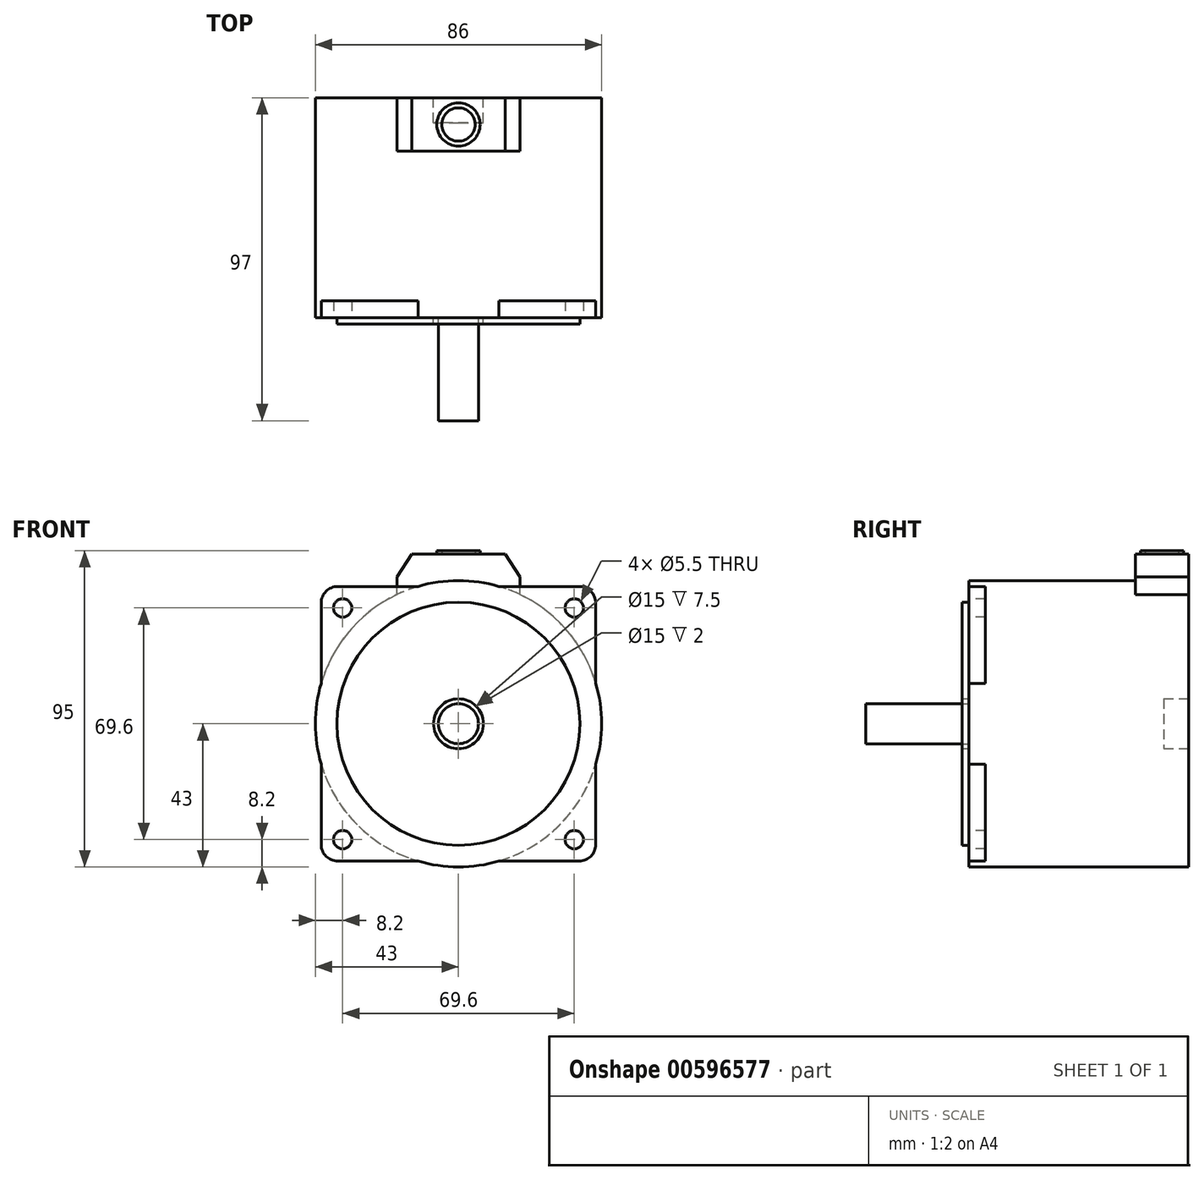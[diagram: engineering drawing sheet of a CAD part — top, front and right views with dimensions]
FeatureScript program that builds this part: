
annotation { "Feature Type Name" : "Feature", "Feature Type Description" : "" }
export const myFeature = defineFeature(function(context is Context, id is Id, definition is map)
    precondition{}
    {
        {
            var Q0;
            Q0=qCreatedBy(makeId("Front.planeOp"),FACE);
            var sketch = newSketch(context, id + "F0", { "sketchPlane" : qUnion([Q0])});
            skCircle(sketch, "E0", {"center": v(0, 0) * mm, "radius": 43 * mm});
            skSolve(sketch);
        }
        {
            var Q0;
            Q0 = qSketchRegion(id + "F0", true);
            extrude(context, id + "F1", {"entities" : qUnion([Q0]), "depth" : 61 * mm, "offsetDistance" : 25 * mm});
        }
        {
            var Q0;
            Q0=makeQuery(id+"F1.opExtrude","CAP_FACE",FACE,{"disambiguationData":[OSD([sQuery(id+"F0.wireOp",EDGE,"E0")])],"isStart":true});
            var sketch = newSketch(context, id + "F2", { "sketchPlane" : qUnion([Q0])});
            skCircle(sketch, "E1", {"center": v(0, 0) * mm, "radius": 7.5 * mm});
            skSolve(sketch);
        }
        {
            var Q0;
            Q0=makeQuery(id+"F2.imprint","IMPRINT",FACE,{"disambiguationData":[TD([[makeQuery(id+"F2.imprint","IMPRINT",EDGE,{"derivedFrom":sQuery(id+"F2.wireOp",EDGE,"E1")}),1.0]])]});
            extrude(context, id + "F3", {"entities" : qUnion([Q0]), "operationType" : NewBodyOperationType.REMOVE, "oppositeDirection" : true, "depth" : 7.5 * mm, "offsetDistance" : 25 * mm});
        }
        {
            var Q0;
            Q0=makeQuery(id+"F1.opExtrude","CAP_FACE",FACE,{"disambiguationData":[OSD([sQuery(id+"F0.wireOp",EDGE,"E0")])],"isStart":false});
            var sketch = newSketch(context, id + "F4", { "sketchPlane" : qUnion([Q0])});
            skLineSegment(sketch, "E2.bottom", {"start": v(-41.25, -41.25) * mm, "end": v(-12.14, -41.25) * mm});
            skLineSegment(sketch, "E2.top", {"start": v(-41.25, 41.25) * mm, "end": v(-12.14, 41.25) * mm});
            skLineSegment(sketch, "E2.left", {"start": v(-41.25, -41.25) * mm, "end": v(-41.25, -12.14) * mm});
            skLineSegment(sketch, "E2.right", {"start": v(41.25, -41.25) * mm, "end": v(41.25, -12.14) * mm});
            skCircle(sketch, "E3", {"center": v(0, 0) * mm, "radius": 43 * mm});
            skLineSegment(sketch, "E4.trimOffspring", {"start": v(12.14, 41.25) * mm, "end": v(41.25, 41.25) * mm});
            skLineSegment(sketch, "E5.trimOffspring", {"start": v(-41.25, 12.14) * mm, "end": v(-41.25, 41.25) * mm});
            skLineSegment(sketch, "E6.trimOffspring", {"start": v(41.25, 12.14) * mm, "end": v(41.25, 41.25) * mm});
            skLineSegment(sketch, "E7.trimOffspring", {"start": v(12.14, -41.25) * mm, "end": v(41.25, -41.25) * mm});
            skSolve(sketch);
        }
        {
            var Q0;
            Q0 = qSketchRegion(id + "F4", true);
            extrude(context, id + "F5", {"entities" : qUnion([Q0]), "operationType" : NewBodyOperationType.ADD, "depth" : 5 * mm, "offsetDistance" : 25 * mm});
        }
        {
            var Q0;
            Q0=makeQuery(id+"F5.opExtrude","SWEPT_EDGE",EDGE,{"disambiguationData":[OSD([sQuery(id+"F4.wireOp",EDGE,"E2.right"),sQuery(id+"F4.wireOp",EDGE,"E7.trimOffspring")])]});
            var Q1;
            Q1=makeQuery(id+"F5.opExtrude","SWEPT_EDGE",EDGE,{"disambiguationData":[OSD([sQuery(id+"F4.wireOp",EDGE,"E2.bottom"),sQuery(id+"F4.wireOp",EDGE,"E2.left")])]});
            var Q2;
            Q2=makeQuery(id+"F5.opExtrude","SWEPT_EDGE",EDGE,{"disambiguationData":[OSD([sQuery(id+"F4.wireOp",EDGE,"E2.top"),sQuery(id+"F4.wireOp",EDGE,"E5.trimOffspring")])]});
            var Q3;
            Q3=makeQuery(id+"F5.opExtrude","SWEPT_EDGE",EDGE,{"disambiguationData":[OSD([sQuery(id+"F4.wireOp",EDGE,"E4.trimOffspring"),sQuery(id+"F4.wireOp",EDGE,"E6.trimOffspring")])]});
            fillet(context, id + "F6", {"entities" : qUnion([Q0, Q1, Q2, Q3]), "radius" : 5 * mm, "tangentPropagation" : true, "allowEdgeOverflow" : false});
        }
        {
            var Q0;
            Q0=makeQuery(id+"F5.opExtrude","CAP_FACE",FACE,{"disambiguationData":[OSD([sQuery(id+"F4.wireOp",EDGE,"E2.bottom"),sQuery(id+"F4.wireOp",EDGE,"E2.top"),sQuery(id+"F4.wireOp",EDGE,"E2.left"),sQuery(id+"F4.wireOp",EDGE,"E2.right"),sQuery(id+"F4.wireOp",EDGE,"E3"),sQuery(id+"F4.wireOp",EDGE,"E4.trimOffspring"),sQuery(id+"F4.wireOp",EDGE,"E5.trimOffspring"),sQuery(id+"F4.wireOp",EDGE,"E6.trimOffspring"),sQuery(id+"F4.wireOp",EDGE,"E7.trimOffspring")])],"isStart":false});
            var sketch = newSketch(context, id + "F7", { "sketchPlane" : qUnion([Q0])});
            skCircle(sketch, "E8", {"center": v(-34.8, 34.8) * mm, "radius": 2.75 * mm});
            skCircle(sketch, "E9.1.0.0", {"center": v(34.8, 34.8) * mm, "radius": 2.75 * mm});
            skLineSegment(sketch, "E9.direction1", {"start": v(-34.8, 34.8) * mm, "end": v(34.8, 34.8) * mm, "construction": true});
            skCircle(sketch, "E10.MirrorC", {"center": v(34.8, -34.8) * mm, "radius": 2.75 * mm});
            skCircle(sketch, "E11.MirrorC", {"center": v(-34.8, -34.8) * mm, "radius": 2.75 * mm});
            skSolve(sketch);
        }
        {
            var Q0;
            Q0 = qSketchRegion(id + "F7", true);
            extrude(context, id + "F8", {"entities" : qUnion([Q0]), "operationType" : NewBodyOperationType.REMOVE, "endBound" : BoundingType.THROUGH_ALL, "oppositeDirection" : true, "depth" : 25 * mm, "offsetDistance" : 25 * mm});
        }
        {
            var Q0;
            Q0=makeQuery(id+"F5.opExtrude","CAP_FACE",FACE,{"disambiguationData":[OSD([sQuery(id+"F4.wireOp",EDGE,"E2.bottom"),sQuery(id+"F4.wireOp",EDGE,"E2.top"),sQuery(id+"F4.wireOp",EDGE,"E2.left"),sQuery(id+"F4.wireOp",EDGE,"E2.right"),sQuery(id+"F4.wireOp",EDGE,"E3"),sQuery(id+"F4.wireOp",EDGE,"E4.trimOffspring"),sQuery(id+"F4.wireOp",EDGE,"E5.trimOffspring"),sQuery(id+"F4.wireOp",EDGE,"E6.trimOffspring"),sQuery(id+"F4.wireOp",EDGE,"E7.trimOffspring")])],"isStart":false});
            var sketch = newSketch(context, id + "F9", { "sketchPlane" : qUnion([Q0])});
            skCircle(sketch, "E12", {"center": v(0, 0) * mm, "radius": 36.5 * mm});
            skCircle(sketch, "E13", {"center": v(0, 0) * mm, "radius": 7.5 * mm});
            skSolve(sketch);
        }
        {
            var Q0;
            Q0=makeQuery(id+"F9.imprint","IMPRINT",FACE,{"disambiguationData":[TD([[makeQuery(id+"F9.imprint","IMPRINT",EDGE,{"derivedFrom":sQuery(id+"F9.wireOp",EDGE,"E12")}),1.0]])]});
            extrude(context, id + "F10", {"entities" : qUnion([Q0]), "operationType" : NewBodyOperationType.ADD, "depth" : 2 * mm, "offsetDistance" : 25 * mm});
        }
        {
            var Q0;
            Q0=makeQuery(id+"F10.boolean.opBoolean","SPLIT",FACE,{"disambiguationData":[TD([makeQuery(id+"F10.opExtrude","SWEPT_FACE",FACE,{"disambiguationData":[OSD([sQuery(id+"F9.wireOp",EDGE,"E13")])]})])],"derivedFrom":makeQuery(id+"F5.opExtrude","CAP_FACE",FACE,{"disambiguationData":[OSD([sQuery(id+"F4.wireOp",EDGE,"E2.bottom"),sQuery(id+"F4.wireOp",EDGE,"E2.top"),sQuery(id+"F4.wireOp",EDGE,"E2.left"),sQuery(id+"F4.wireOp",EDGE,"E2.right"),sQuery(id+"F4.wireOp",EDGE,"E3"),sQuery(id+"F4.wireOp",EDGE,"E4.trimOffspring"),sQuery(id+"F4.wireOp",EDGE,"E5.trimOffspring"),sQuery(id+"F4.wireOp",EDGE,"E6.trimOffspring"),sQuery(id+"F4.wireOp",EDGE,"E7.trimOffspring")])],"isStart":false})});
            var sketch = newSketch(context, id + "F11", { "sketchPlane" : qUnion([Q0])});
            skCircle(sketch, "E14", {"center": v(0, 0) * mm, "radius": 6 * mm});
            skSolve(sketch);
        }
        {
            var Q0;
            Q0 = qSketchRegion(id + "F11", true);
            extrude(context, id + "F12", {"entities" : qUnion([Q0]), "operationType" : NewBodyOperationType.ADD, "depth" : 31 * mm, "offsetDistance" : 25 * mm});
        }
        {
            var Q0;
            Q0=makeQuery(id+"F1.opExtrude","CAP_FACE",FACE,{"disambiguationData":[OSD([sQuery(id+"F0.wireOp",EDGE,"E0")])],"isStart":true});
            var sketch = newSketch(context, id + "F13", { "sketchPlane" : qUnion([Q0])});
            skLineSegment(sketch, "E15", {"start": v(0, 0) * mm, "end": v(0, 51) * mm, "construction": true});
            skLineSegment(sketch, "E16.0", {"start": v(-18.5, 38.82) * mm, "end": v(-18.5, 44.1) * mm});
            skLineSegment(sketch, "E17.MirrorCS", {"start": v(18.5, 38.82) * mm, "end": v(18.5, 44.1) * mm});
            skLineSegment(sketch, "E18.0", {"start": v(14, 51) * mm, "end": v(0, 51) * mm});
            skLineSegment(sketch, "E19.MirrorCS", {"start": v(-14, 51) * mm, "end": v(0, 51) * mm});
            skLineSegment(sketch, "E20", {"start": v(-18.5, 44.1) * mm, "end": v(-14, 51) * mm});
            skPoint(sketch, "E21.orphan", {"position": v(-18.5, 51) * mm});
            skLineSegment(sketch, "E22.MirrorCS", {"start": v(18.5, 44.1) * mm, "end": v(14, 51) * mm});
            skPoint(sketch, "E23.orphan", {"position": v(18.5, 51) * mm});
            skArc(sketch, "E24", {"start": v(18.5, 38.82) * mm, "mid": v(0, 43) * mm, "end": v(-18.5, 38.82) * mm});
            skPoint(sketch, "E25.orphan", {"position": v(-18.5, 0) * mm});
            skPoint(sketch, "E26.orphan", {"position": v(18.5, 0) * mm});
            skSolve(sketch);
        }
        {
            var Q0;
            Q0=makeQuery(id+"F13.imprint","IMPRINT",FACE,{"disambiguationData":[TD([[makeQuery(id+"F13.imprint","IMPRINT",EDGE,{"derivedFrom":sQuery(id+"F13.wireOp",EDGE,"E16.0")}),-1.0]])]});
            extrude(context, id + "F14", {"entities" : qUnion([Q0]), "operationType" : NewBodyOperationType.ADD, "oppositeDirection" : true, "depth" : 16 * mm, "offsetDistance" : 25 * mm});
        }
        {
            var Q0;
            Q0=makeQuery(id+"F14.opExtrude","SWEPT_FACE",FACE,{"disambiguationData":[OSD([sQuery(id+"F13.wireOp",EDGE,"E18.0"),sQuery(id+"F13.wireOp",EDGE,"E19.MirrorCS")])]});
            var sketch = newSketch(context, id + "F15", { "sketchPlane" : qUnion([Q0])});
            skCircle(sketch, "E27", {"center": v(0, -8) * mm, "radius": 6.5 * mm});
            skPoint(sketch, "E27.centerSnap0", {"position": v(14, -8) * mm});
            skCircle(sketch, "E28", {"center": v(0, -8) * mm, "radius": 5 * mm});
            skSolve(sketch);
        }
        {
            var Q0;
            Q0 = qSketchRegion(id + "F15", true);
            extrude(context, id + "F16", {"entities" : qUnion([Q0]), "operationType" : NewBodyOperationType.ADD, "depth" : 1 * mm, "offsetDistance" : 25 * mm});
        }
    });
